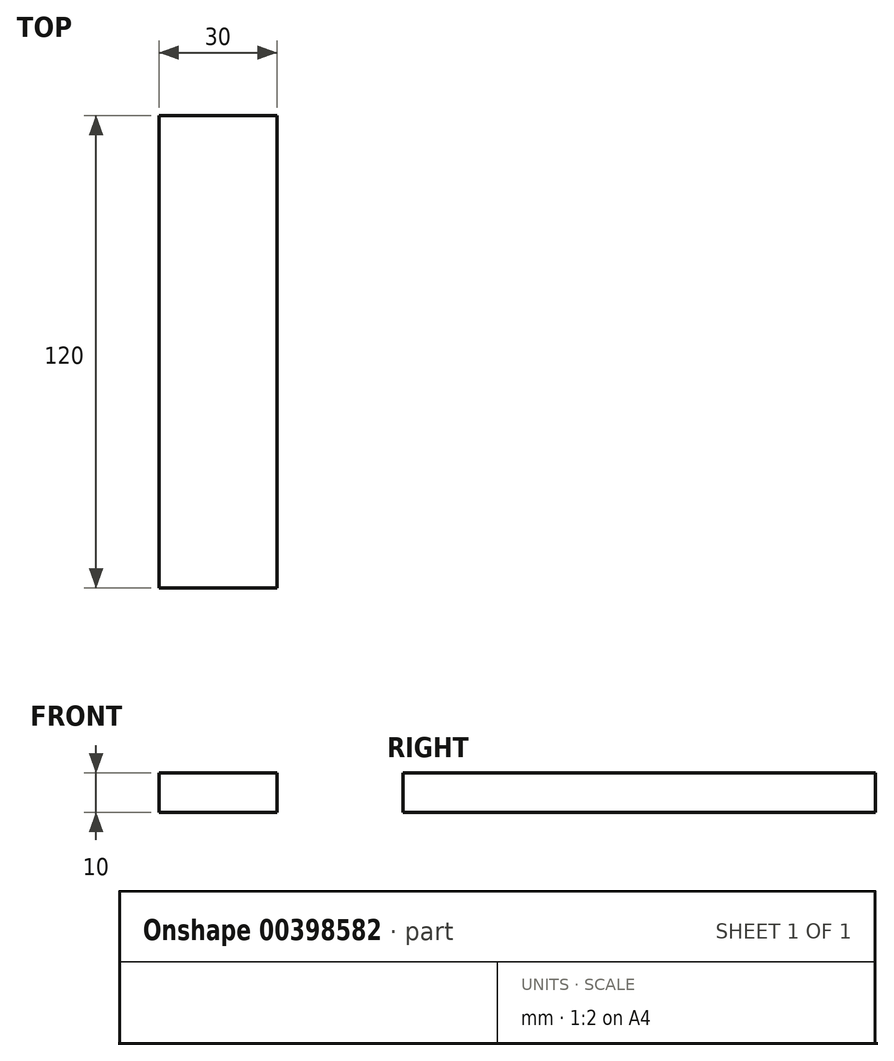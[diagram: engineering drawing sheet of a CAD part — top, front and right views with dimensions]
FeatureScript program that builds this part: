
annotation { "Feature Type Name" : "Feature", "Feature Type Description" : "" }
export const myFeature = defineFeature(function(context is Context, id is Id, definition is map)
    precondition{}
    {
        {
            var Q0;
            Q0=qCreatedBy(makeId("Front.planeOp"),FACE);
            var sketch = newSketch(context, id + "F0", { "sketchPlane" : qUnion([Q0])});
            skLineSegment(sketch, "E0.bottom", {"start": v(-9.9, 7.81) * mm, "end": v(20.1, 7.81) * mm});
            skLineSegment(sketch, "E0.top", {"start": v(-9.9, -2.19) * mm, "end": v(20.1, -2.19) * mm});
            skLineSegment(sketch, "E0.left", {"start": v(-9.9, 7.81) * mm, "end": v(-9.9, -2.19) * mm});
            skLineSegment(sketch, "E0.right", {"start": v(20.1, 7.81) * mm, "end": v(20.1, -2.19) * mm});
            skSolve(sketch);
        }
        {
            var Q0;
            Q0 = qSketchRegion(id + "F0", true);
            extrude(context, id + "F1", {"entities" : qUnion([Q0]), "depth" : 120 * mm});
        }
    });
